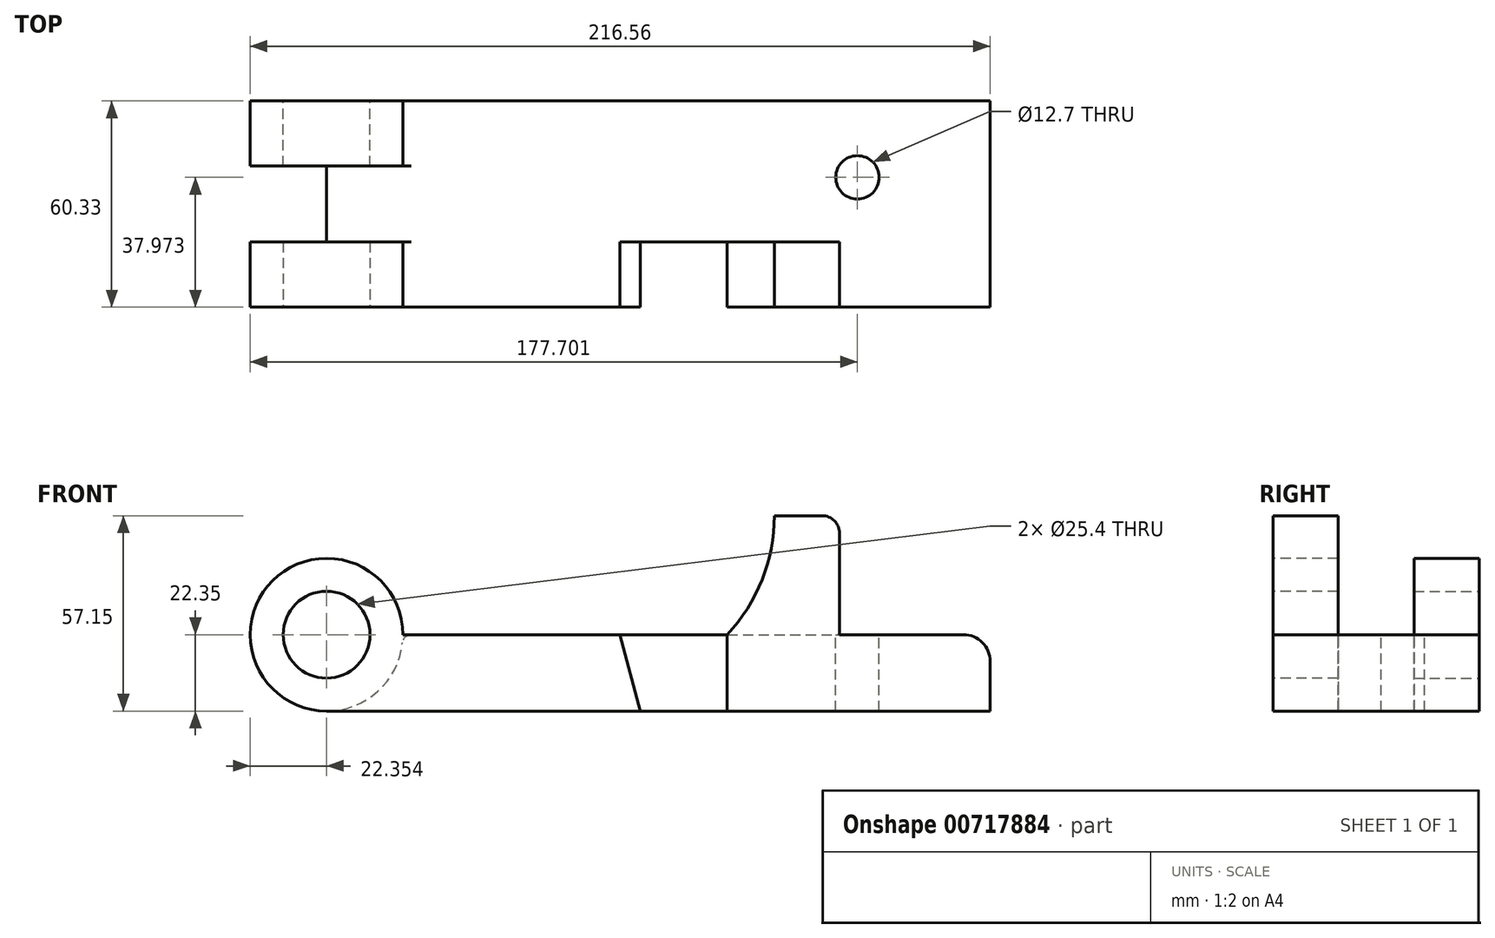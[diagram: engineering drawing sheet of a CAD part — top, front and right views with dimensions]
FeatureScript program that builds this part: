
annotation { "Feature Type Name" : "Feature", "Feature Type Description" : "" }
export const myFeature = defineFeature(function(context is Context, id is Id, definition is map)
    precondition{}
    {
        {
            var Q0;
            Q0=qCreatedBy(makeId("Front.planeOp"),FACE);
            var sketch = newSketch(context, id + "F0", { "sketchPlane" : qUnion([Q0])});
            skCircle(sketch, "E0", {"center": v(-60.72, 0) * mm, "radius": 12.7 * mm});
            skCircle(sketch, "E1", {"center": v(-60.72, 0) * mm, "radius": 22.35 * mm});
            skPoint(sketch, "E2", {"position": v(-83.07, 0) * mm});
            skLineSegment(sketch, "E3", {"start": v(-38.36, 0) * mm, "end": v(25.14, 0) * mm});
            skLineSegment(sketch, "E4", {"start": v(25.14, 0) * mm, "end": v(70.32, 0) * mm});
            skLineSegment(sketch, "E5", {"start": v(70.32, 0) * mm, "end": v(133.5, 0) * mm});
            skLineSegment(sketch, "E6", {"start": v(-60.72, 0) * mm, "end": v(-60.72, -22.35) * mm});
            skLineSegment(sketch, "E7", {"start": v(-60.72, -22.35) * mm, "end": v(133.5, -22.35) * mm});
            skLineSegment(sketch, "E8", {"start": v(133.5, -22.35) * mm, "end": v(133.5, 0) * mm});
            skLineSegment(sketch, "E9", {"start": v(25.14, 0) * mm, "end": v(31.13, -22.35) * mm});
            skLineSegment(sketch, "E10", {"start": v(56.53, 0) * mm, "end": v(56.53, -22.35) * mm});
            skPoint(sketch, "E11", {"position": v(89.37, 0) * mm});
            skLineSegment(sketch, "E12", {"start": v(70.32, 0) * mm, "end": v(70.32, 34.8) * mm});
            skLineSegment(sketch, "E13", {"start": v(89.37, 0) * mm, "end": v(89.37, 34.8) * mm});
            skLineSegment(sketch, "E14", {"start": v(89.37, 34.8) * mm, "end": v(70.32, 34.8) * mm});
            skArc(sketch, "E15", {"start": v(56.53, 0) * mm, "mid": v(66.75, 16.08) * mm, "end": v(70.32, 34.8) * mm});
            skSolve(sketch);
        }
        {
            var Q0;
            {var subQ0=sQuery(id+"F0.wireOp",EDGE,"E3");Q0=makeQuery(id+"F0.imprint","IMPRINT",FACE,{"disambiguationData":[TD([[makeQuery(id+"F0.imprint","IMPRINT",EDGE,{"derivedFrom":subQ0}),-1.0]])]});}
            var Q1;
            {var subQ0=sQuery(id+"F0.wireOp",EDGE,"E9");Q1=makeQuery(id+"F0.imprint","IMPRINT",FACE,{"disambiguationData":[TD([[makeQuery(id+"F0.imprint","IMPRINT",EDGE,{"derivedFrom":subQ0}),1.0]])]});}
            var Q2;
            {var subQ0=sQuery(id+"F0.wireOp",EDGE,"E8");Q2=makeQuery(id+"F0.imprint","IMPRINT",FACE,{"disambiguationData":[TD([[makeQuery(id+"F0.imprint","IMPRINT",EDGE,{"derivedFrom":subQ0}),1.0]])]});}
            extrude(context, id + "F1", {"entities" : qUnion([Q0, Q1, Q2]), "oppositeDirection" : true, "depth" : 60.32 * mm, "offsetDistance" : 25.4 * mm});
        }
        {
            var Q0;
            {var subQ0=sQuery(id+"F0.wireOp",EDGE,"E9");Q0=makeQuery(id+"F0.imprint","IMPRINT",FACE,{"disambiguationData":[TD([[makeQuery(id+"F0.imprint","IMPRINT",EDGE,{"derivedFrom":subQ0}),1.0]])]});}
            extrude(context, id + "F2", {"entities" : qUnion([Q0]), "operationType" : NewBodyOperationType.REMOVE, "oppositeDirection" : true, "depth" : 19.05 * mm, "offsetDistance" : 25.4 * mm});
        }
        {
            var Q0;
            {var subQ0=sQuery(id+"F0.wireOp",EDGE,"E12");Q0=makeQuery(id+"F0.imprint","IMPRINT",FACE,{"disambiguationData":[TD([[makeQuery(id+"F0.imprint","IMPRINT",EDGE,{"derivedFrom":subQ0}),1.0]])]});}
            var Q1;
            {var subQ0=sQuery(id+"F0.wireOp",EDGE,"E12");Q1=makeQuery(id+"F0.imprint","IMPRINT",FACE,{"disambiguationData":[TD([[makeQuery(id+"F0.imprint","IMPRINT",EDGE,{"derivedFrom":subQ0}),-1.0]])]});}
            extrude(context, id + "F3", {"entities" : qUnion([Q0, Q1]), "operationType" : NewBodyOperationType.ADD, "oppositeDirection" : true, "depth" : 19.05 * mm, "offsetDistance" : 25.4 * mm});
        }
        {
            var Q0;
            Q0=makeQuery(id+"F0.imprint","IMPRINT",FACE,{"disambiguationData":[TD([[makeQuery(id+"F0.imprint","IMPRINT",EDGE,{"derivedFrom":sQuery(id+"F0.wireOp",EDGE,"E0")}),-1.0]])]});
            extrude(context, id + "F4", {"entities" : qUnion([Q0]), "oppositeDirection" : true, "depth" : 19.05 * mm, "offsetDistance" : 25.4 * mm});
        }
        {
            var Q0;
            Q0=qCreatedBy(makeId("Front.planeOp"),FACE);
            cPlane(context, id + "F5", {"entities" : qUnion([Q0]), "cplaneType" : CPlaneType.OFFSET, "offset" : 30.16 * mm, "oppositeDirection" : true, "width" : 152.4 * mm, "height" : 152.4 * mm});
        }
        {
            var Q0;
            Q0=makeQuery(id+"F4.opExtrude","SWEPT_BODY",BODY,{"disambiguationData":[OSD([sQuery(id+"F0.wireOp",EDGE,"E0"),sQuery(id+"F0.wireOp",EDGE,"E1")])]});
            var Q1;
            Q1=qCreatedBy(id+"F5.planeOp",FACE);
            mirror(context, id + "F6", {"entities" : qUnion([Q0]), "mirrorPlane" : qUnion([Q1])});
        }
        {
            var Q0;
            Q0=makeQuery(id+"F1.opExtrude","SWEPT_BODY",BODY,{"disambiguationData":[OSD([sQuery(id+"F0.wireOp",EDGE,"E1"),sQuery(id+"F0.wireOp",EDGE,"E3"),sQuery(id+"F0.wireOp",EDGE,"E4"),sQuery(id+"F0.wireOp",EDGE,"E5"),sQuery(id+"F0.wireOp",EDGE,"E7"),sQuery(id+"F0.wireOp",EDGE,"E8")])]});
            var Q1;
            Q1=makeQuery(id+"F4.opExtrude","SWEPT_BODY",BODY,{"disambiguationData":[OSD([sQuery(id+"F0.wireOp",EDGE,"E0"),sQuery(id+"F0.wireOp",EDGE,"E1")])]});
            var Q2;
            Q2=makeQuery(id+"F6.opPattern","COPY",BODY,{"derivedFrom":makeQuery(id+"F4.opExtrude","SWEPT_BODY",BODY,{"disambiguationData":[OSD([sQuery(id+"F0.wireOp",EDGE,"E0"),sQuery(id+"F0.wireOp",EDGE,"E1")])]}),"instanceName":"1"});
            booleanBodies(context, id + "F7", {"operationType" : BooleanOperationType.UNION, "tools" : qUnion([Q0, Q1, Q2])});
        }
        {
            var Q0;
            Q0=makeQuery(id+"F1.opExtrude","SWEPT_FACE",FACE,{"disambiguationData":[OSD([sQuery(id+"F0.wireOp",EDGE,"E3"),sQuery(id+"F0.wireOp",EDGE,"E4"),sQuery(id+"F0.wireOp",EDGE,"E5")])]});
            var sketch = newSketch(context, id + "F8", { "sketchPlane" : qUnion([Q0])});
            skPoint(sketch, "E16", {"position": v(133.5, 60.33) * mm});
            skLineSegment(sketch, "E17", {"start": v(133.5, 60.33) * mm, "end": v(94.63, 60.33) * mm, "construction": true});
            skLineSegment(sketch, "E18", {"start": v(94.63, 60.33) * mm, "end": v(94.63, 37.97) * mm, "construction": true});
            skCircle(sketch, "E19", {"center": v(94.63, 37.97) * mm, "radius": 6.35 * mm});
            skSolve(sketch);
        }
        {
            var Q0;
            Q0=makeQuery(id+"F8.imprint","IMPRINT",FACE,{"disambiguationData":[TD([[makeQuery(id+"F8.imprint","IMPRINT",EDGE,{"derivedFrom":sQuery(id+"F8.wireOp",EDGE,"E19")}),1.0]])]});
            extrude(context, id + "F9", {"entities" : qUnion([Q0]), "operationType" : NewBodyOperationType.REMOVE, "oppositeDirection" : true, "depth" : 25.4 * mm, "offsetDistance" : 25.4 * mm});
        }
        {
            var Q0;
            Q0=makeQuery(id+"F1.opExtrude","SWEPT_EDGE",EDGE,{"disambiguationData":[OSD([sQuery(id+"F0.wireOp",EDGE,"E5"),sQuery(id+"F0.wireOp",EDGE,"E8")])]});
            fillet(context, id + "F10", {"entities" : qUnion([Q0]), "radius" : 7.87 * mm, "tangentPropagation" : true, "allowEdgeOverflow" : false});
        }
        {
            var Q0;
            Q0=makeQuery(id+"F3.opExtrude","SWEPT_EDGE",EDGE,{"disambiguationData":[OSD([sQuery(id+"F0.wireOp",EDGE,"E13"),sQuery(id+"F0.wireOp",EDGE,"E14")])]});
            fillet(context, id + "F11", {"entities" : qUnion([Q0]), "radius" : 5.08 * mm, "tangentPropagation" : true, "allowEdgeOverflow" : false});
        }
        {
            var Q0;
            {var subQ0=sQuery(id+"F0.wireOp",EDGE,"E3");var subQ1=sQuery(id+"F0.wireOp",EDGE,"E1");Q0=makeQuery(id+"F7.opBoolean","SPLIT",EDGE,{"disambiguationData":[topologyDisambiguationEdgeConnected([makeQuery(id+"F6.opPattern","COPY",FACE,{"derivedFrom":makeQuery(id+"F4.opExtrude","SWEPT_FACE",FACE,{"disambiguationData":[OSD([subQ1])]}),"instanceName":"1"})])],"derivedFrom":makeQuery(id+"F1.opExtrude","SWEPT_EDGE",EDGE,{"disambiguationData":[OSD([subQ1,subQ0])]})});}
            var Q1;
            {var subQ0=sQuery(id+"F0.wireOp",EDGE,"E3");var subQ1=sQuery(id+"F0.wireOp",EDGE,"E1");Q1=makeQuery(id+"F7.opBoolean","SPLIT",EDGE,{"disambiguationData":[topologyDisambiguationEdgeConnected([makeQuery(id+"F4.opExtrude","SWEPT_FACE",FACE,{"disambiguationData":[OSD([subQ1])]})])],"derivedFrom":makeQuery(id+"F1.opExtrude","SWEPT_EDGE",EDGE,{"disambiguationData":[OSD([subQ1,subQ0])]})});}
            var Q2;
            Q2=makeQuery(id+"F3.opExtrude","SWEPT_EDGE",EDGE,{"disambiguationData":[OSD([sQuery(id+"F0.wireOp",EDGE,"E5"),sQuery(id+"F0.wireOp",EDGE,"E13")])]});
            fillet(context, id + "F12", {"entities" : qUnion([Q0, Q1, Q2]), "radius" : 2.54 * mm, "tangentPropagation" : true, "allowEdgeOverflow" : false});
        }
    });
